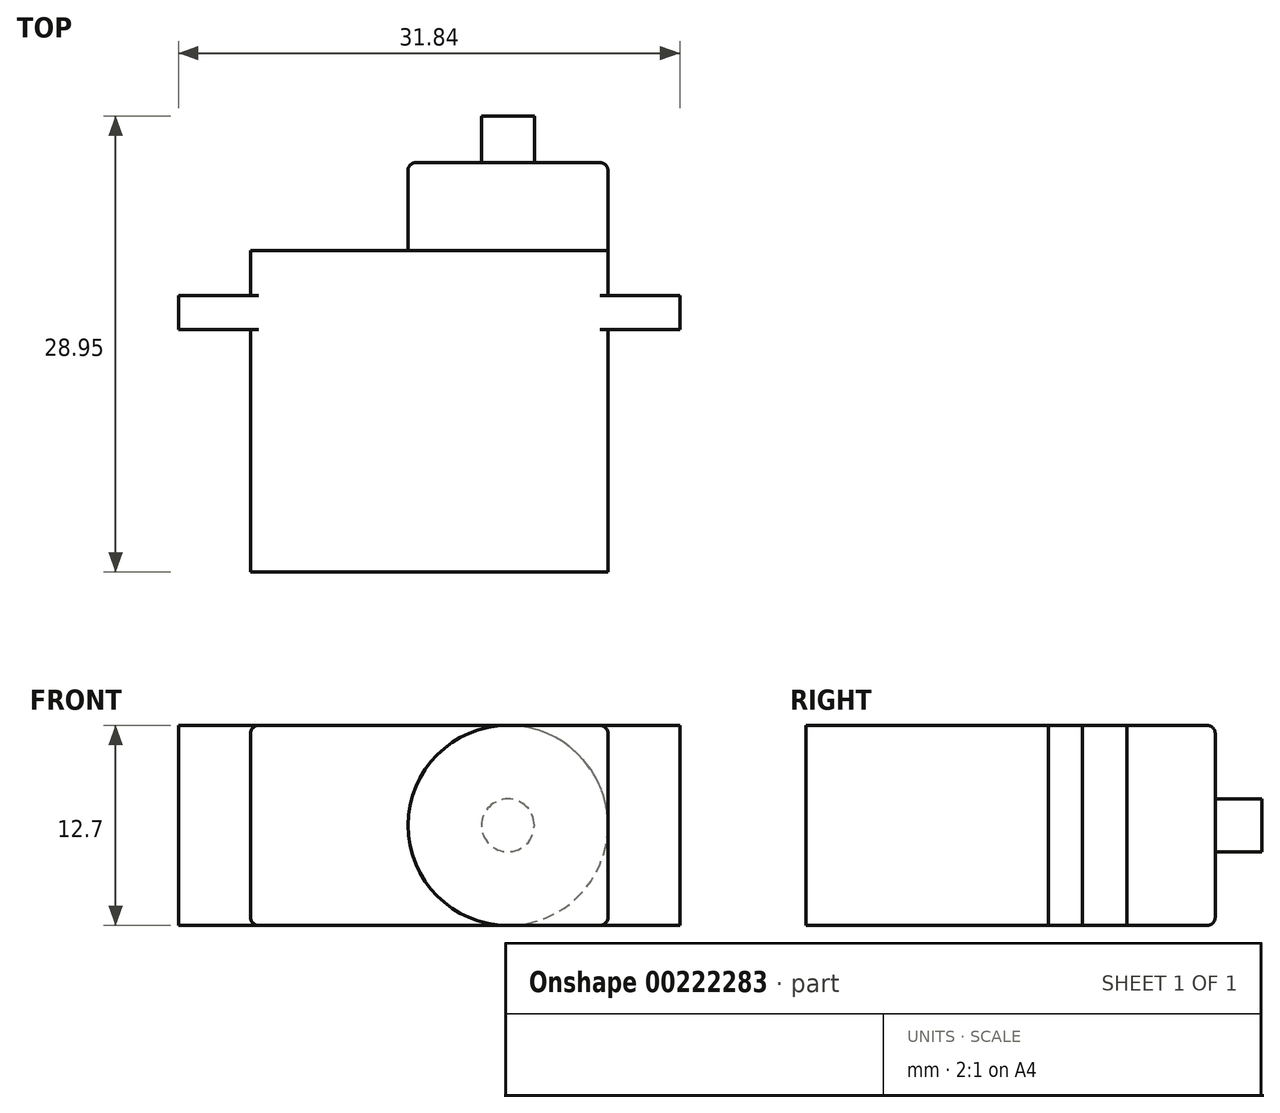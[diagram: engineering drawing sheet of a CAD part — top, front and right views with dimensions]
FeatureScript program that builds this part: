
annotation { "Feature Type Name" : "Feature", "Feature Type Description" : "" }
export const myFeature = defineFeature(function(context is Context, id is Id, definition is map)
    precondition{}
    {
        {
            assignVariable(context, id + "F0", {"name" : "boxDepth", "anyValue" : 12.7});
        }
        {
            assignVariable(context, id + "F1", {"name" : "servoKnobHeight", "anyValue" : 5.6});
        }
        {
            var Q0;
            Q0=qCreatedBy(makeId("Top.planeOp"),FACE);
            var sketch = newSketch(context, id + "F2", { "sketchPlane" : qUnion([Q0])});
            skLineSegment(sketch, "E0.bottom", {"start": v(-11.35, 20.4) * mm, "end": v(11.35, 20.4) * mm});
            skLineSegment(sketch, "E0.top", {"start": v(-11.35, 0) * mm, "end": v(11.35, 0) * mm});
            skLineSegment(sketch, "E0.left", {"start": v(-11.35, 20.4) * mm, "end": v(-11.35, 17.55) * mm});
            skLineSegment(sketch, "E0.right", {"start": v(11.35, 20.4) * mm, "end": v(11.35, 17.55) * mm});
            skLineSegment(sketch, "E1.bottom", {"start": v(15.92, 17.55) * mm, "end": v(11.35, 17.55) * mm});
            skLineSegment(sketch, "E1.top", {"start": v(15.92, 15.4) * mm, "end": v(11.35, 15.4) * mm});
            skLineSegment(sketch, "E1.left", {"start": v(15.92, 17.55) * mm, "end": v(15.92, 15.4) * mm});
            skLineSegment(sketch, "E1.right", {"start": v(-15.92, 17.55) * mm, "end": v(-15.92, 15.4) * mm});
            skLineSegment(sketch, "E2.trimOffspring", {"start": v(-11.35, 17.55) * mm, "end": v(-15.92, 17.55) * mm});
            skLineSegment(sketch, "E3.trimOffspring", {"start": v(-11.35, 15.4) * mm, "end": v(-15.92, 15.4) * mm});
            skLineSegment(sketch, "E4.trimOffspring", {"start": v(-11.35, 15.4) * mm, "end": v(-11.35, 0) * mm});
            skLineSegment(sketch, "E5.trimOffspring", {"start": v(11.35, 15.4) * mm, "end": v(11.35, 0) * mm});
            skSolve(sketch);
        }
        {
            var Q0;
            Q0 = qSketchRegion(id + "F2", true);
            extrude(context, id + "F3", {"entities" : qUnion([Q0]), "depth" : (getVariable(context, 'boxDepth')) * mm});
        }
        {
            var Q0;
            Q0=makeQuery(id+"F3.opExtrude","CAP_EDGE",EDGE,{"disambiguationData":[OSD([sQuery(id+"F2.wireOp",EDGE,"E5.trimOffspring")])],"isStart":false});
            var Q1;
            Q1=makeQuery(id+"F3.opExtrude","CAP_EDGE",EDGE,{"disambiguationData":[OSD([sQuery(id+"F2.wireOp",EDGE,"E0.right")])],"isStart":false});
            var Q2;
            Q2=makeQuery(id+"F3.opExtrude","CAP_EDGE",EDGE,{"disambiguationData":[OSD([sQuery(id+"F2.wireOp",EDGE,"E0.right")])],"isStart":true});
            var Q3;
            Q3=makeQuery(id+"F3.opExtrude","CAP_EDGE",EDGE,{"disambiguationData":[OSD([sQuery(id+"F2.wireOp",EDGE,"E5.trimOffspring")])],"isStart":true});
            var Q4;
            Q4=makeQuery(id+"F3.opExtrude","CAP_EDGE",EDGE,{"disambiguationData":[OSD([sQuery(id+"F2.wireOp",EDGE,"E0.left")])],"isStart":false});
            var Q5;
            Q5=makeQuery(id+"F3.opExtrude","CAP_EDGE",EDGE,{"disambiguationData":[OSD([sQuery(id+"F2.wireOp",EDGE,"E4.trimOffspring")])],"isStart":false});
            var Q6;
            Q6=makeQuery(id+"F3.opExtrude","CAP_EDGE",EDGE,{"disambiguationData":[OSD([sQuery(id+"F2.wireOp",EDGE,"E0.left")])],"isStart":true});
            var Q7;
            Q7=makeQuery(id+"F3.opExtrude","CAP_EDGE",EDGE,{"disambiguationData":[OSD([sQuery(id+"F2.wireOp",EDGE,"E4.trimOffspring")])],"isStart":true});
            fillet(context, id + "F4", {"entities" : qUnion([Q0, Q1, Q2, Q3, Q4, Q5, Q6, Q7]), "radius" : 0.5 * mm, "tangentPropagation" : true, "allowEdgeOverflow" : false});
        }
        {
            var Q0;
            Q0=makeQuery(id+"F3.opExtrude","SWEPT_FACE",FACE,{"disambiguationData":[OSD([sQuery(id+"F2.wireOp",EDGE,"E0.bottom")])]});
            cPlane(context, id + "F5", {"entities" : qUnion([Q0]), "cplaneType" : CPlaneType.OFFSET, "offset" : 0 * mm, "width" : 150 * mm, "height" : 150 * mm});
        }
        {
            var Q0;
            Q0=qCreatedBy(id+"F5.planeOp",FACE);
            var sketch = newSketch(context, id + "F6", { "sketchPlane" : qUnion([Q0])});
            skCircle(sketch, "E6", {"center": v(-5, 6.35) * mm, "radius": 6.35 * mm});
            skSolve(sketch);
        }
        {
            var Q0;
            Q0 = qSketchRegion(id + "F6", true);
            extrude(context, id + "F7", {"entities" : qUnion([Q0]), "operationType" : NewBodyOperationType.ADD, "depth" : (getVariable(context, 'servoKnobHeight')) * mm});
        }
        {
            var Q0;
            Q0=makeQuery(id+"F7.opExtrude","CAP_EDGE",EDGE,{"disambiguationData":[OSD([sQuery(id+"F6.wireOp",EDGE,"E6")])],"isStart":false});
            fillet(context, id + "F8", {"entities" : qUnion([Q0]), "radius" : 0.5 * mm, "tangentPropagation" : true, "allowEdgeOverflow" : false});
        }
        {
            var Q0;
            Q0=makeQuery(id+"F7.opExtrude","CAP_FACE",FACE,{"disambiguationData":[OSD([sQuery(id+"F6.wireOp",EDGE,"E6")])],"isStart":false});
            var sketch = newSketch(context, id + "F9", { "sketchPlane" : qUnion([Q0])});
            skCircle(sketch, "E7", {"center": v(-5, 6.35) * mm, "radius": 1.67 * mm});
            skSolve(sketch);
        }
        {
            var Q0;
            Q0=makeQuery(id+"F9.imprint","IMPRINT",FACE,{"disambiguationData":[TD([[makeQuery(id+"F9.imprint","IMPRINT",EDGE,{"derivedFrom":sQuery(id+"F9.wireOp",EDGE,"E7")}),1.0]])]});
            var Q1;
            Q1=sQuery(id+"F9.wireOp",EDGE,"E7");
            extrude(context, id + "F10", {"entities" : qUnion([Q0]), "operationType" : NewBodyOperationType.ADD, "surfaceEntities" : qUnion([Q1]), "depth" : 2.95 * mm});
        }
    });
